# Revit family: fire_rinnai_compact2
name_source: partatom
category: Specialty Equipment
revit_build: Autodesk Revit 2015 (Build: 20140905_0730(x64)
units: mm (PartAtom-declared; Revit-internal decimal feet)

## types (2) — shared parameters
Manufacturer = Rinnai NZ Ltd
Model = Compact 2
_fire_centrewidth = 550 mm
_fire_clearceiling = 1000 mm  [stored 3.28084 ft]
_fire_cleardepth = 1000 mm  [stored 3.28084 ft]
_fire_clearheight = 300 mm
_fire_clearwidth = 1100 mm
_fire_side_clearance = 300 mm
_fire_top = 640 mm  [stored 2.09974 ft]
_fire_width = 750 mm  [stored 2.46063 ft]
_fire_window_top = 420 mm  [stored 1.37795 ft]
_fire_window_width = 500 mm  [stored 1.64042 ft]
_opening_height = 615 mm  [stored 2.01772 ft]
_opening_width = 685 mm
clearance = 5 mm  [stored 0.0164042 ft]
m_plinth = <By Category>
opening floor offset = 45 mm  [stored 0.147638 ft]
v_fireplace = Yes

## per-type parameters (varying)
| type | Description | URL | _opening_depth |
| compact2_masonry | Compact 2 Masonry | www.rinnai.co.nz. | 360 mm  [stored 1.1811 ft] |
| compact2_mock | Compact 2 Mock | www.rinnai.co.nz | 380 mm  [stored 1.24672 ft] |

note: [stored X ft] marks values corroborated as IEEE doubles in the binary element streams (Revit-internal decimal feet)

## geometry (parser evidence)
native form markers: Sweep x27
no freeform markers — native parametric forms only
